# Revit family: 1
name_source: partatom
category: Doors
revit_build: Autodesk Revit 2015 (Build: 20140606_1530(x64)
units: mm (PartAtom-declared; Revit-internal decimal feet)

## types (1)
- MEGAPACK
    Analytic Construction = <None>
    BIMobject category = Industrial
    BIMobject category code = doors-industrial
    BIMobject main category = Doors
    BIMobject main category code = doors
    Brand url = http://www.bmpdoors.com
    Design country = Italy
    Edition number = 1
    Function = Interior
    Height = 22800 mm
    IFC Classification = Door
    Manufacturer country = Italy
    Manufacturer name = BMP Europe
    Masterformat 2014 Code = 08 11 16
    Masterformat 2014 Description = Aluminum Doors and Frames
    Material Steel = Metal- BMP - Steel
    Material main = Aluminium
    NBS Reference Code = 25-30-20-20
    NBS Reference Description = Doorset Systems
    Nominal height = 0 mm  [stored 0 ft]
    Nominal width = 0 mm  [stored 0 ft]
    OmniClass Code = 23-17 11 45 17
    OmniClass Description = Rapid Opening Doors
    Product Guid = 6ccebd75-dbae-484a-bc39-563181c18cca
    Product SKU = MEGAPACK
    Product data url = https://bimobject.com
    Product family = Doors / Industrial
    Product group = Fold-up doors - Megaimpack
    Product url = http://www.bmpeurope.eu
    QR code = http://bimobject.com
    Technical description = https://s3-eu-west-1.amazonaws.com
    UNSPSC Code = 30171503
    Uniclass 1.4 Code = JL20
    Uniclass 1.4 Description = Doors
    Uniclass 2.0 Code = SS-25-30-20-20
    Uniclass 2.0 Description = Doorset Systems
    Uniclass 2015 Code = Pr_30_59_24_04
    Uniclass 2015 Name = Automatic revolving doorsets
    Uniformat II Code = B2030
    Uniformat II Description = Exterior Doors
    Wall Closure = By host
    Weight Net (Kg) = 0
    Width = 20240 mm

note: [stored X ft] marks values corroborated as IEEE doubles in the binary element streams (Revit-internal decimal feet)

## geometry (parser evidence)
native form markers: Sweep x21
no freeform markers — native parametric forms only
